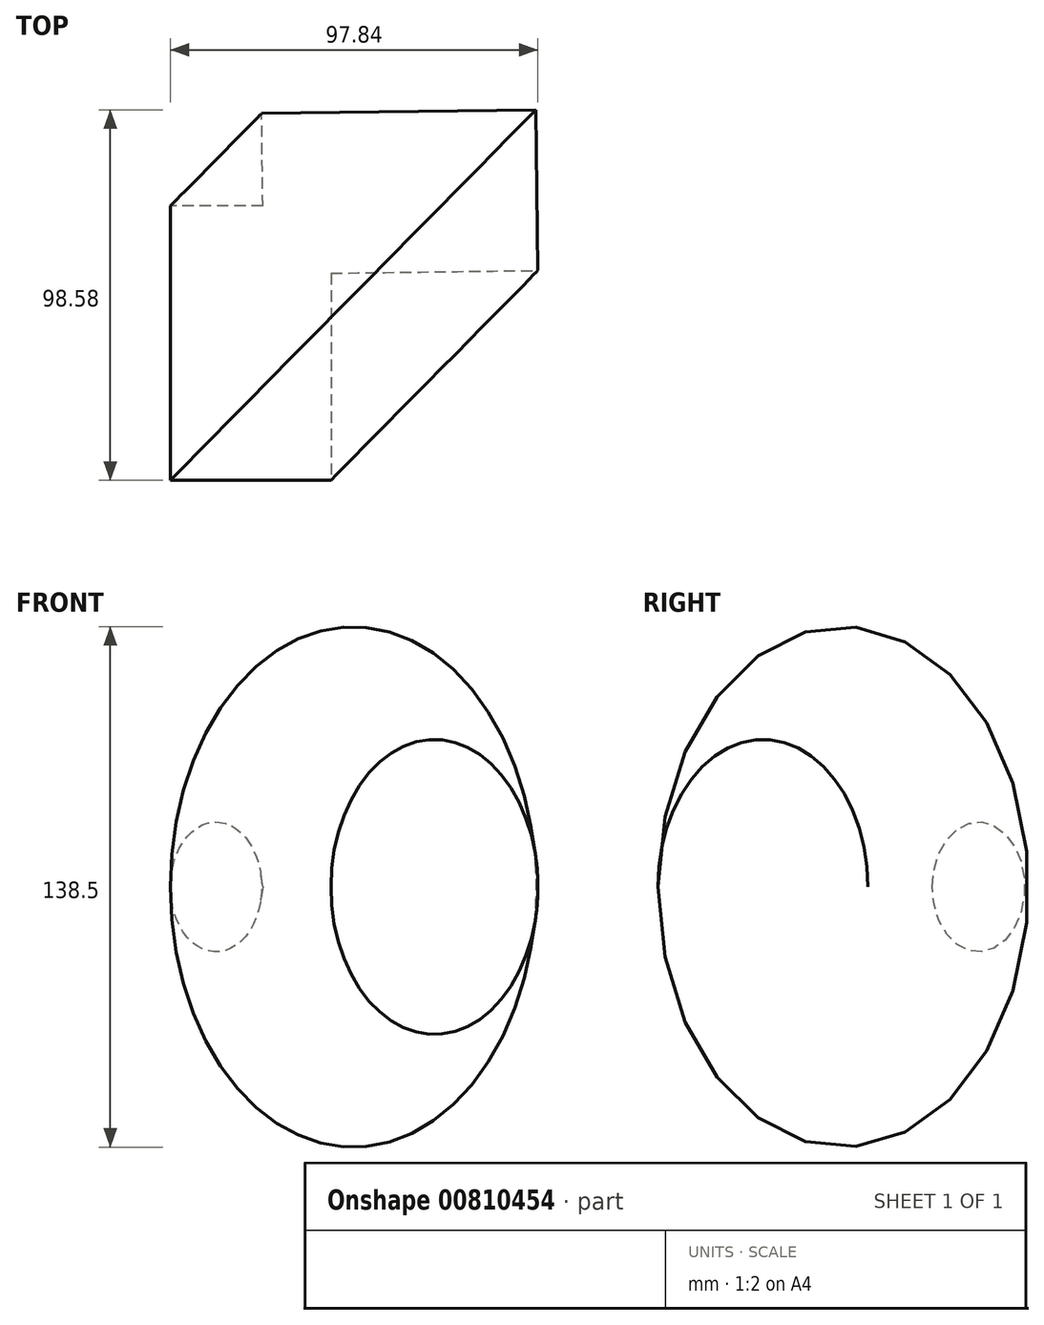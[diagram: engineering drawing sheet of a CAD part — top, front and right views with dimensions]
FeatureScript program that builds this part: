
annotation { "Feature Type Name" : "Feature", "Feature Type Description" : "" }
export const myFeature = defineFeature(function(context is Context, id is Id, definition is map)
    precondition{}
    {
        {
            var Q0;
            Q0=qCreatedBy(makeId("Top.planeOp"),FACE);
            var sketch = newSketch(context, id + "F0", { "sketchPlane" : qUnion([Q0])});
            skLineSegment(sketch, "E0.bottom", {"start": v(-19.4, 48.4) * mm, "end": v(23.36, 48.4) * mm});
            skLineSegment(sketch, "E0.top", {"start": v(-19.4, -24.58) * mm, "end": v(23.36, -24.58) * mm});
            skLineSegment(sketch, "E0.left", {"start": v(-19.4, 48.4) * mm, "end": v(-19.4, -24.58) * mm});
            skLineSegment(sketch, "E0.right", {"start": v(23.36, 48.4) * mm, "end": v(23.36, -24.58) * mm});
            skLineSegment(sketch, "E1", {"start": v(-9, 62.45) * mm, "end": v(36.8, 17.25) * mm});
            skSolve(sketch);
        }
        {
            var Q0;
            {var subQ1=sQuery(id+"F0.wireOp",EDGE,"E0.top");Q0=makeQuery(id+"F0.imprint","IMPRINT",FACE,{"disambiguationData":[TD([[makeQuery(id+"F0.imprint","IMPRINT",EDGE,{"derivedFrom":subQ1}),1.0]])]});}
            var Q1;
            Q1=sQuery(id+"F0.wireOp",EDGE,"E1");
            revolve(context, id + "F1", {"surfaceOperationType" : NewSurfaceOperationType.NEW, "entities" : qUnion([Q0]), "axis" : qUnion([Q1]), "revolveType" : RevolveType.FULL});
        }
    });
